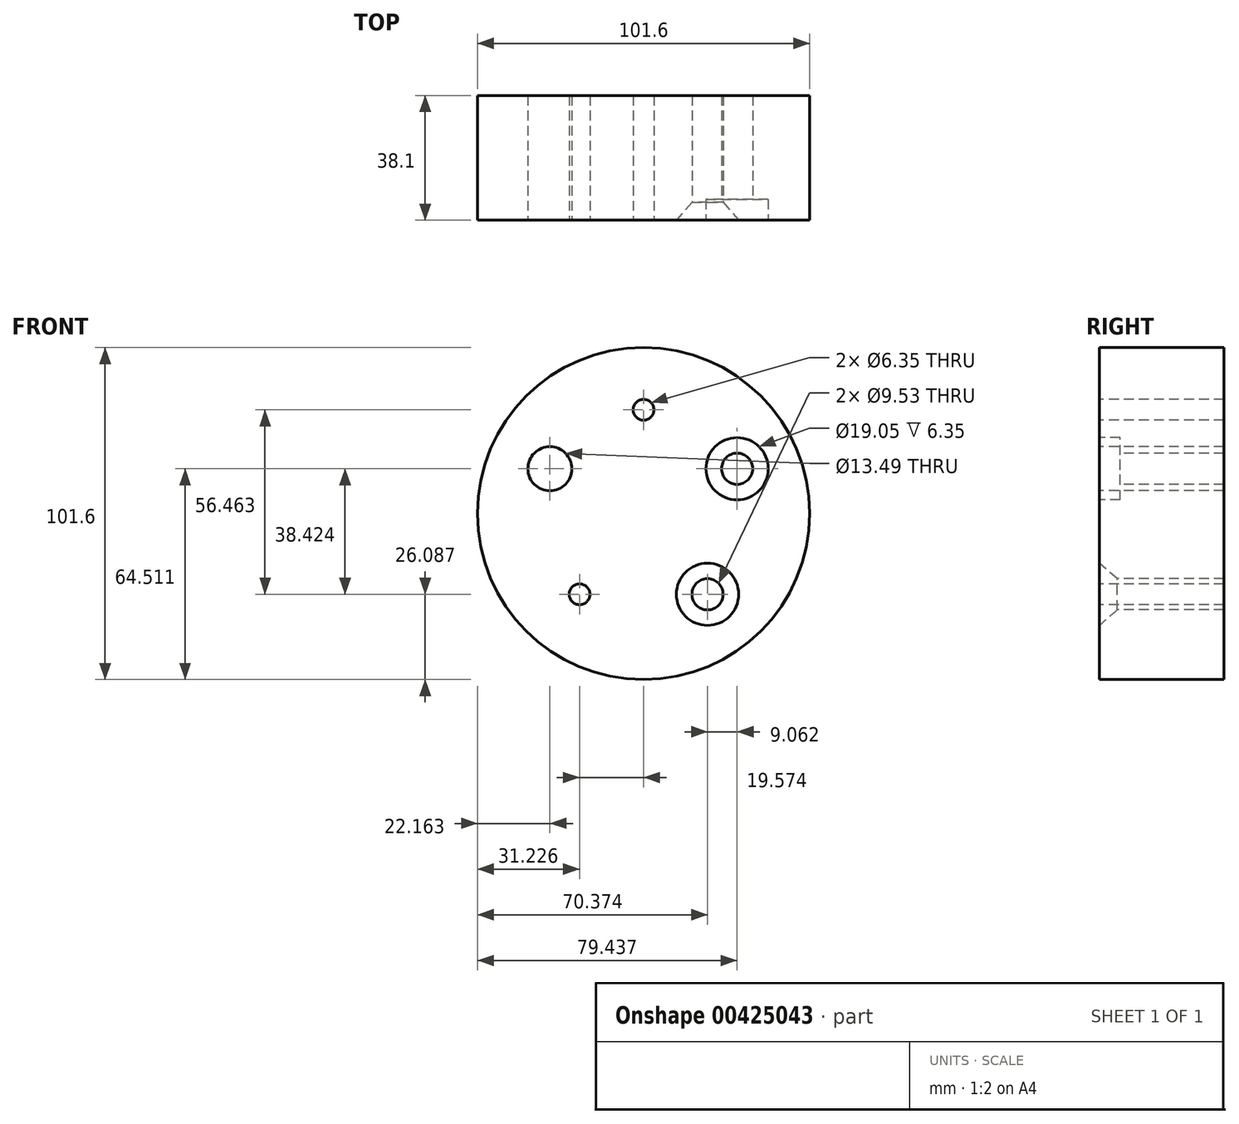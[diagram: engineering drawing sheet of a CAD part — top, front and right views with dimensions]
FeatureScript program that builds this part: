
annotation { "Feature Type Name" : "Feature", "Feature Type Description" : "" }
export const myFeature = defineFeature(function(context is Context, id is Id, definition is map)
    precondition{}
    {
        {
            var Q0;
            Q0=qCreatedBy(makeId("Front.planeOp"),FACE);
            var sketch = newSketch(context, id + "F0", { "sketchPlane" : qUnion([Q0])});
            skCircle(sketch, "E0", {"center": v(0, 0) * mm, "radius": 50.8 * mm});
            skLineSegment(sketch, "E1", {"start": v(0, 0) * mm, "end": v(0, 31.75) * mm});
            skCircle(sketch, "E2", {"center": v(0, 0) * mm, "radius": 31.75 * mm});
            skSolve(sketch);
        }
        {
            var Q0;
            Q0=makeQuery(id+"F0.imprint","IMPRINT",FACE,{"disambiguationData":[TD([[makeQuery(id+"F0.imprint","IMPRINT",EDGE,{"derivedFrom":sQuery(id+"F0.wireOp",EDGE,"E0")}),1.0]])]});
            var Q1;
            Q1=makeQuery(id+"F0.imprint","IMPRINT",FACE,{"disambiguationData":[TD([[makeQuery(id+"F0.imprint","IMPRINT",EDGE,{"derivedFrom":sQuery(id+"F0.wireOp",EDGE,"E2")}),1.0]])]});
            extrude(context, id + "F1", {"entities" : qUnion([Q0, Q1]), "depth" : 38.1 * mm});
        }
        {
            var Q0;
            Q0=makeQuery(id+"F1.opExtrude","CAP_FACE",FACE,{"disambiguationData":[OSD([sQuery(id+"F0.wireOp",EDGE,"E0")])],"isStart":false});
            var sketch = newSketch(context, id + "F2", { "sketchPlane" : qUnion([Q0])});
            skPoint(sketch, "E3", {"position": v(0, 31.75) * mm});
            skPoint(sketch, "E4", {"position": v(28.64, 13.71) * mm});
            skPoint(sketch, "E5", {"position": v(-28.64, 13.71) * mm});
            skPoint(sketch, "E6", {"position": v(-19.57, -24.71) * mm});
            skPoint(sketch, "E7", {"position": v(19.57, -24.71) * mm});
            skSolve(sketch);
        }
        {
            var Q0;
            Q0=sQuery(id+"F2.wireOp",VERTEX,"E3");
            var Q1;
            Q1=makeQuery(id+"F1.opExtrude","SWEPT_BODY",BODY,{"disambiguationData":[OSD([sQuery(id+"F0.wireOp",EDGE,"E0")])]});
            hole(context, id + "F3", {"style" : HoleStyle.SIMPLE, "endStyle" : HoleEndStyle.THROUGH, "holeDiameter" : 6.35 * mm, "isTappedThrough" : true, "tappedDepth" : 12.7 * mm, "tapClearance" : 3, "locations" : qUnion([Q0]), "scope" : qUnion([Q1])});
        }
        {
            var Q0;
            Q0=sQuery(id+"F2.wireOp",VERTEX,"E4");
            var Q1;
            Q1=makeQuery(id+"F1.opExtrude","SWEPT_BODY",BODY,{"disambiguationData":[OSD([sQuery(id+"F0.wireOp",EDGE,"E0")])]});
            hole(context, id + "F4", {"style" : HoleStyle.C_BORE, "endStyle" : HoleEndStyle.THROUGH, "holeDiameter" : 9.52 * mm, "cBoreDiameter" : 19.05 * mm, "cBoreDepth" : 6.35 * mm, "isTappedThrough" : true, "tappedDepth" : 12.7 * mm, "tapClearance" : 3, "locations" : qUnion([Q0]), "scope" : qUnion([Q1])});
        }
        {
            var Q0;
            Q0=sQuery(id+"F2.wireOp",VERTEX,"E7");
            var Q1;
            Q1=makeQuery(id+"F1.opExtrude","SWEPT_BODY",BODY,{"disambiguationData":[OSD([sQuery(id+"F0.wireOp",EDGE,"E0")])]});
            hole(context, id + "F5", {"style" : HoleStyle.C_SINK, "endStyle" : HoleEndStyle.THROUGH, "holeDiameter" : 9.52 * mm, "cSinkDiameter" : 19.05 * mm, "cSinkAngle" : 82 * degree, "isTappedThrough" : true, "tappedDepth" : 12.7 * mm, "tapClearance" : 3, "locations" : qUnion([Q0]), "scope" : qUnion([Q1])});
        }
        {
            var Q0;
            Q0=sQuery(id+"F2.wireOp",VERTEX,"E6");
            var Q1;
            Q1=makeQuery(id+"F1.opExtrude","SWEPT_BODY",BODY,{"disambiguationData":[OSD([sQuery(id+"F0.wireOp",EDGE,"E0")])]});
            hole(context, id + "F6", {"style" : HoleStyle.SIMPLE, "endStyle" : HoleEndStyle.THROUGH, "holeDiameter" : 6.35 * mm, "isTappedThrough" : true, "tappedDepth" : 12.7 * mm, "tapClearance" : 3, "locations" : qUnion([Q0]), "scope" : qUnion([Q1])});
        }
        {
            var Q0;
            Q0=sQuery(id+"F2.wireOp",VERTEX,"E5");
            var Q1;
            Q1=makeQuery(id+"F1.opExtrude","SWEPT_BODY",BODY,{"disambiguationData":[OSD([sQuery(id+"F0.wireOp",EDGE,"E0")])]});
            hole(context, id + "F7", {"style" : HoleStyle.SIMPLE, "endStyle" : HoleEndStyle.THROUGH, "holeDiameter" : 13.5 * mm, "isTappedThrough" : true, "tappedDepth" : 12.7 * mm, "tapClearance" : 3, "locations" : qUnion([Q0]), "scope" : qUnion([Q1])});
        }
    });
